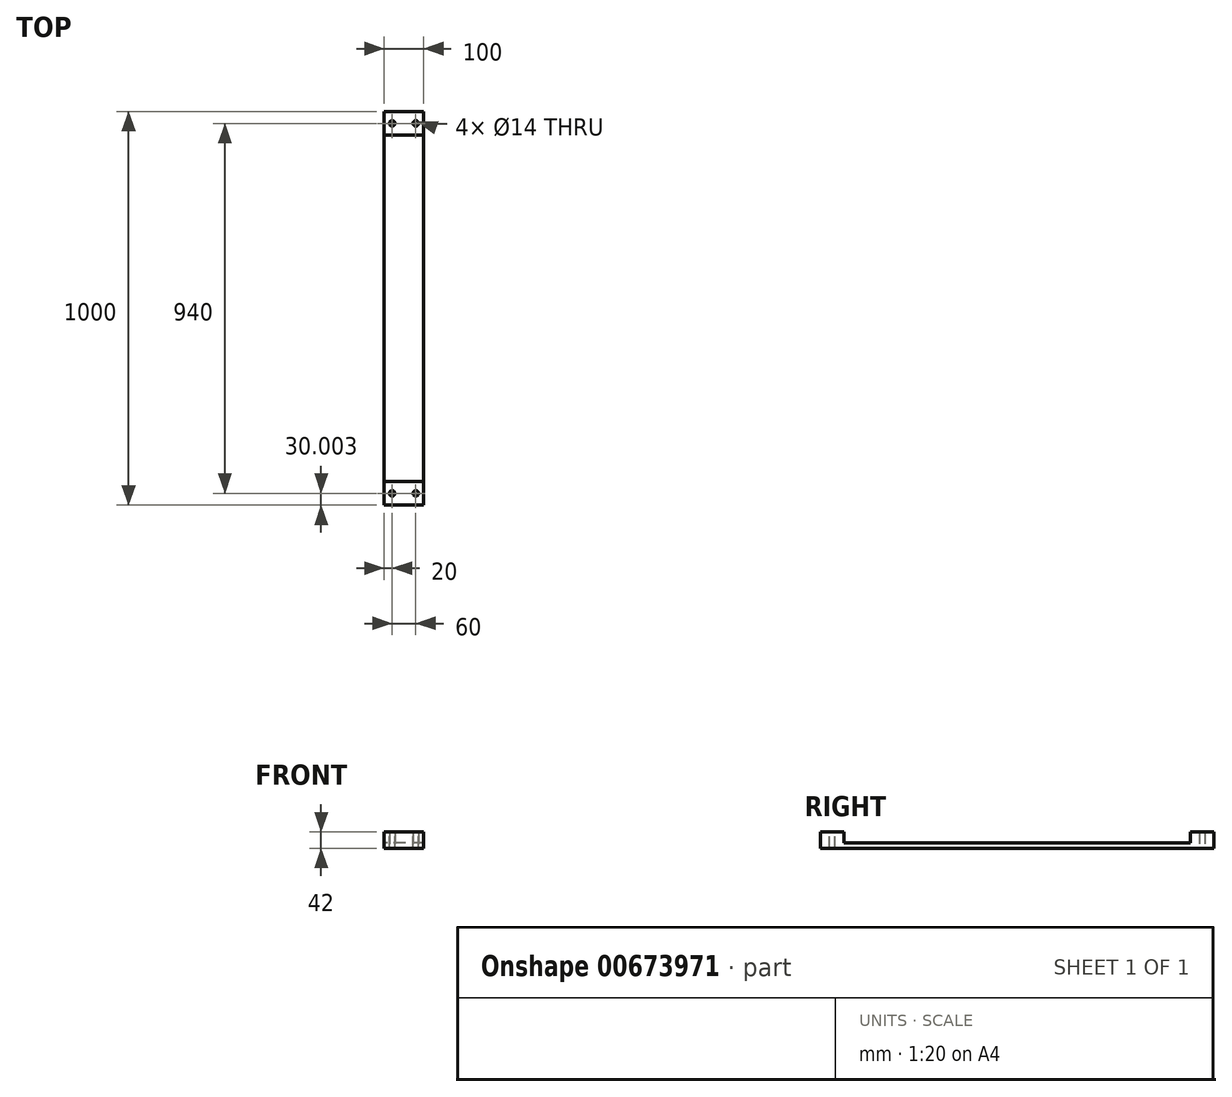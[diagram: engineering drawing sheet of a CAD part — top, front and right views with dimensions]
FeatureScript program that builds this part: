
annotation { "Feature Type Name" : "Feature", "Feature Type Description" : "" }
export const myFeature = defineFeature(function(context is Context, id is Id, definition is map)
    precondition{}
    {
        {
            var Q0;
            Q0=qCreatedBy(makeId("Right.planeOp"),FACE);
            var sketch = newSketch(context, id + "F0", { "sketchPlane" : qUnion([Q0])});
            skLineSegment(sketch, "E0", {"start": v(-502.92, 0) * mm, "end": v(497.08, 0) * mm});
            skLineSegment(sketch, "E1.0", {"start": v(-502.92, 14) * mm, "end": v(497.08, 14) * mm});
            skLineSegment(sketch, "E2", {"start": v(-502.92, 14) * mm, "end": v(-502.92, 0) * mm});
            skLineSegment(sketch, "E3", {"start": v(497.08, 14) * mm, "end": v(497.08, 0) * mm});
            skLineSegment(sketch, "E4.bottom", {"start": v(-502.92, 14) * mm, "end": v(-442.92, 14) * mm});
            skLineSegment(sketch, "E4.top", {"start": v(-502.92, 42) * mm, "end": v(-442.92, 42) * mm});
            skLineSegment(sketch, "E4.left", {"start": v(-502.92, 14) * mm, "end": v(-502.92, 42) * mm});
            skLineSegment(sketch, "E4.right", {"start": v(-442.92, 14) * mm, "end": v(-442.92, 42) * mm});
            skLineSegment(sketch, "E5.bottom", {"start": v(497.08, 14) * mm, "end": v(437.08, 14) * mm});
            skLineSegment(sketch, "E5.top", {"start": v(497.08, 42) * mm, "end": v(437.08, 42) * mm});
            skLineSegment(sketch, "E5.left", {"start": v(497.08, 14) * mm, "end": v(497.08, 42) * mm});
            skLineSegment(sketch, "E5.right", {"start": v(437.08, 14) * mm, "end": v(437.08, 42) * mm});
            skSolve(sketch);
        }
        {
            var Q0;
            Q0 = qSketchRegion(id + "F0", true);
            extrude(context, id + "F1", {"entities" : qUnion([Q0]), "endBound" : BoundingType.SYMMETRIC, "depth" : 100 * mm, "offsetDistance" : 25 * mm});
        }
        {
            var Q0;
            Q0=makeQuery(id+"F1.opExtrude","SWEPT_FACE",FACE,{"disambiguationData":[OSD([sQuery(id+"F0.wireOp",EDGE,"E4.top")])]});
            var sketch = newSketch(context, id + "F2", { "sketchPlane" : qUnion([Q0])});
            skCircle(sketch, "E6", {"center": v(-30, -472.92) * mm, "radius": 7 * mm});
            skCircle(sketch, "E7.MirrorC", {"center": v(30, -472.92) * mm, "radius": 7 * mm});
            skLineSegment(sketch, "E8", {"start": v(-30, -472.92) * mm, "end": v(30, -472.92) * mm});
            skSolve(sketch);
        }
        {
            var Q0;
            Q0 = qSketchRegion(id + "F2", true);
            extrude(context, id + "F3", {"entities" : qUnion([Q0]), "operationType" : NewBodyOperationType.REMOVE, "endBound" : BoundingType.SYMMETRIC, "oppositeDirection" : true, "depth" : 100 * mm, "offsetDistance" : 25 * mm});
        }
        {
            var Q0;
            Q0=makeQuery(id+"F1.opExtrude","SWEPT_FACE",FACE,{"disambiguationData":[OSD([sQuery(id+"F0.wireOp",EDGE,"E5.top")])]});
            var sketch = newSketch(context, id + "F4", { "sketchPlane" : qUnion([Q0])});
            skCircle(sketch, "E9", {"center": v(-30, 467.08) * mm, "radius": 7 * mm});
            skCircle(sketch, "E10.MirrorC", {"center": v(30, 467.08) * mm, "radius": 7 * mm});
            skLineSegment(sketch, "E11", {"start": v(-30, 467.08) * mm, "end": v(30, 467.08) * mm});
            skSolve(sketch);
        }
        {
            var Q0;
            Q0 = qSketchRegion(id + "F4", true);
            extrude(context, id + "F5", {"entities" : qUnion([Q0]), "operationType" : NewBodyOperationType.REMOVE, "endBound" : BoundingType.SYMMETRIC, "depth" : 100 * mm, "offsetDistance" : 25 * mm});
        }
    });
